# Revit family: Flowerpot table lamp VP3
name_source: partatom
category: Furniture
revit_build: Autodesk Revit 2017 (Build: 20171027_0315(x64)
units: mm (PartAtom-declared; Revit-internal decimal feet)

## family parameters
Always vertical = Yes
Cut with Voids When Loaded = No
OmniClass Number = 23.40.20.00
OmniClass Title = General Furniture and Specialties
Room Calculation Point = No
Shared = No
Work Plane-Based = No

## types (1)
- Flowerpot table lamp VP3
    Cord = &tradition Plastic White Matt
    Description = The Flowerpot, a vividly coloured lamp with a rounded pendant that hangs from the semi-domed upper shade, embodies the experimental attitude of Verner Panton. Slightly smaller in size than the table lamp version, and deliberately lightweight, the portable VP9 comes equipped with a USB charging cable. It is available in a wide range of contemporary colours.
    Design = Verner Panton
    Design Year = 1968
    Diameter = 23cm / 9.1in
    Height = 50cm / 19.7in
    Lamp Base = &tradition Laquered metal - Stone Blue (NCS S 6005-B80G)
    Lamp Bottom = &tradition Plastic Stone Blue (NCS S 6005-B80G)
    Lamp Shade bearing = &tradition Plastic White Matt
    Lamp feet = &tradition Textile cord - Stone Blue (NCS S 6005-B80G)
    Lamp shade = &tradition Laquered metal - Stone Blue (NCS S 6005-B80G)
    Lamp shade inside = &tradition Powder Coated Aluminium white
    Lamp top = &tradition Chrome
    Manufacturer = &tradition
    Model = Flowerpot VP3
    Packaging Dimensions = H55.0cm/21.7in, W27.0cm/10.6in, D27.0cm/10.6in
    Socket = &tradition Plastic White Matt
    URL = https://www.andtradition.com
    Variations = Dark Green, Mustard, Beige Red, Grey Beige, White, Matt Black, Matt White, Matt Light Grey, Light Blue, Red Brown, Polished Stainless Steel, Polished Brass
    Weight = 4.55kg

## geometry (parser evidence)
native form markers: Sweep x2
no freeform markers — native parametric forms only
